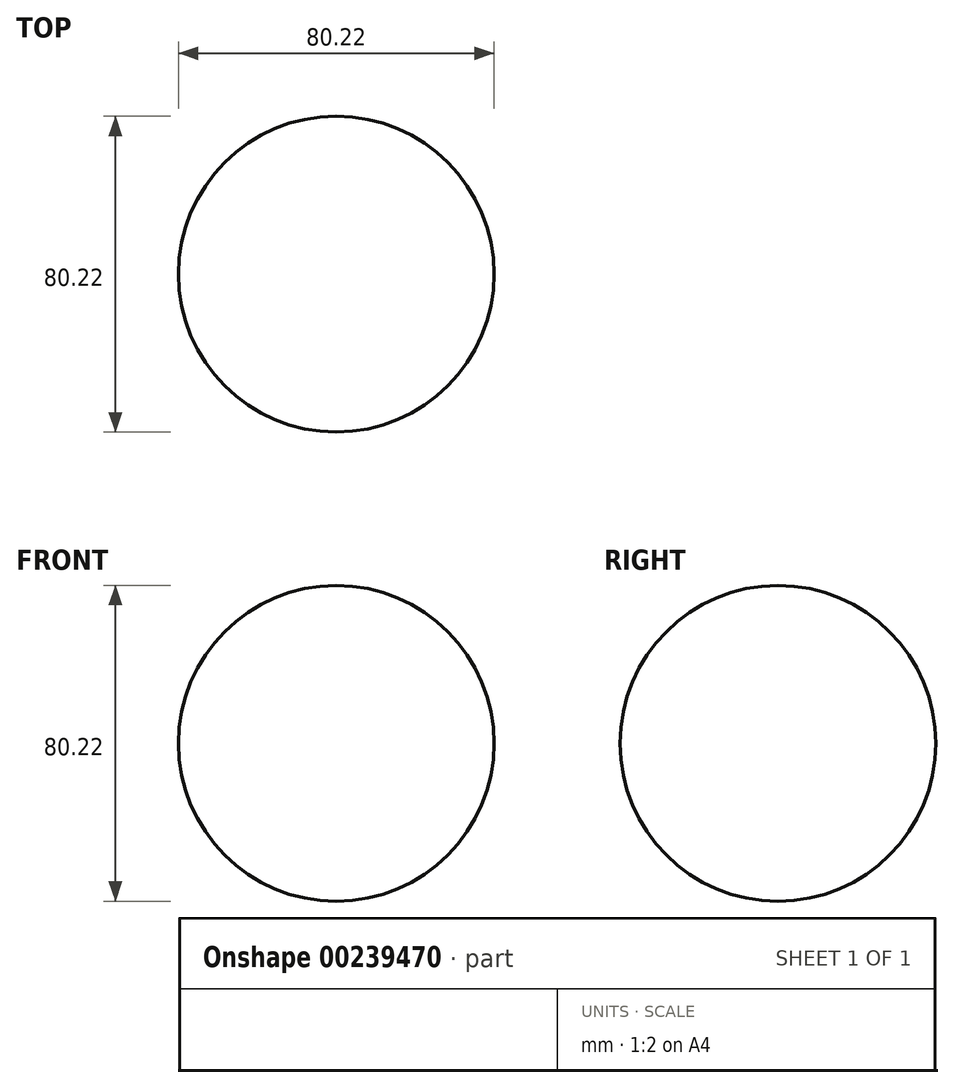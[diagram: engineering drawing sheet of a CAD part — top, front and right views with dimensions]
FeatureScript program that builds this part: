
annotation { "Feature Type Name" : "Feature", "Feature Type Description" : "" }
export const myFeature = defineFeature(function(context is Context, id is Id, definition is map)
    precondition{}
    {
        {
            var Q0;
            Q0=qCreatedBy(makeId("Front.planeOp"),FACE);
            var sketch = newSketch(context, id + "F0", { "sketchPlane" : qUnion([Q0])});
            skArc(sketch, "E0", {"start": v(0, -40.11) * mm, "mid": v(40.11, 0) * mm, "end": v(0, 40.11) * mm});
            skLineSegment(sketch, "E1", {"start": v(0, 40.11) * mm, "end": v(0, -40.11) * mm});
            skSolve(sketch);
        }
        {
            var Q0;
            Q0 = qSketchRegion(id + "F0", true);
            var Q1;
            Q1=sQuery(id+"F0.wireOp",EDGE,"E1");
            revolve(context, id + "F1", {"entities" : qUnion([Q0]), "axis" : qUnion([Q1]), "revolveType" : RevolveType.FULL});
        }
    });
